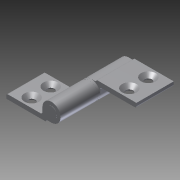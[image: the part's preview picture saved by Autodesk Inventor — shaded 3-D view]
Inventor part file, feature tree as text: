
AUTODESK INVENTOR PART (.ipt)
format: ipt  version: 2011 SP1 (Build 150282100, 282)  size: 165,888 bytes
history: native  units: mm
features: other x42, sketch x8, extrude x4, hole x4
ambient origin geometry x8: Origin, YZ Plane, XZ Plane, XY Plane, X Axis, Y Axis, Z Axis, Center Point
bodies: Solid1 (feature_tree)
feature tree (58):
  extrude  "Extrusion1"  Depth=85.5mm TaperAngle=0.0deg
  extrude  "Extrusion2"  Depth=41.25mm TaperAngle=0.0deg
  extrude  "Extrusion3"  [1 undecoded]
  extrude  "Extrusion4"  [1 undecoded]
  hole  "Drilling 1"  [1 undecoded]
  hole  "Drilling 2"  [1 undecoded]
  hole  "Drilling 3"  [1 undecoded]
  hole  "Drilling 4"  [1 undecoded]
  other  "side_2a_XY"
  other  "side_2a_YZ"
  other  "side_2a_ZX"
  other  "side_2a_X"
  other  "side_2a_Y"
  other  "side_2a_Z"
  other  "side_2a_Center"
  other  "side_2b_XY"
  other  "side_2b_YZ"
  other  "side_2b_ZX"
  other  "side_2b_X"
  other  "side_2b_Y"
  other  "side_2b_Z"
  other  "side_2b_Center"
  other  "side_1b_XY"
  other  "side_1b_YZ"
  other  "side_1b_ZX"
  other  "side_1b_X"
  other  "side_1b_Y"
  other  "side_1b_Z"
  other  "side_1b_Center"
  other  "side_3b_XY"
  other  "side_3b_YZ"
  other  "side_3b_ZX"
  other  "side_3b_X"
  other  "side_3b_Y"
  other  "side_3b_Z"
  other  "side_3b_Center"
  other  "side_1a_XY"
  other  "side_1a_YZ"
  other  "side_1a_ZX"
  other  "side_1a_X"
  other  "side_1a_Y"
  other  "side_1a_Z"
  other  "side_1a_Center"
  other  "side_3a_XY"
  other  "side_3a_YZ"
  other  "side_3a_ZX"
  other  "side_3a_X"
  other  "side_3a_Y"
  other  "side_3a_Z"
  other  "side_3a_Center"
  sketch  "Skizze_34"  dims[d22=8.0mm d23=6.0mm d24=16.0mm d25=2.0mm d26=15.707963mm d27=5.0mm d28=0.0mm]
  sketch  "Skizze_35"  dims[d29=8.0mm d30=6.0mm d31=16.0mm d32=2.0mm d33=15.707963mm d34=5.0mm d35=0.0mm]
  sketch  "Skizze_36"
  sketch  "Skizze_37"
  sketch  "Sketch5"  dims[d0=2.5mm d1=0.0mm d2=85.5mm d3=0.0mm]
  sketch  "Sketch6"  dims[d4=41.25mm d5=0.0mm d6=41.25mm d7=0.0mm]
  sketch  "Sketch7"  dims[d8=8.0mm d9=6.0mm d10=16.0mm d11=2.0mm d12=15.707963mm d13=5.0mm d14=0.0mm]
  sketch  "Sketch8"  dims[d15=8.0mm d16=6.0mm d17=16.0mm d18=2.0mm d19=15.707963mm d20=5.0mm d21=0.0mm]
note: 6 required parameter values undecoded (feature->parameter linkage not recoverable at this tier; creation-order binding heuristic only, values carry confidence <= 0.55)
